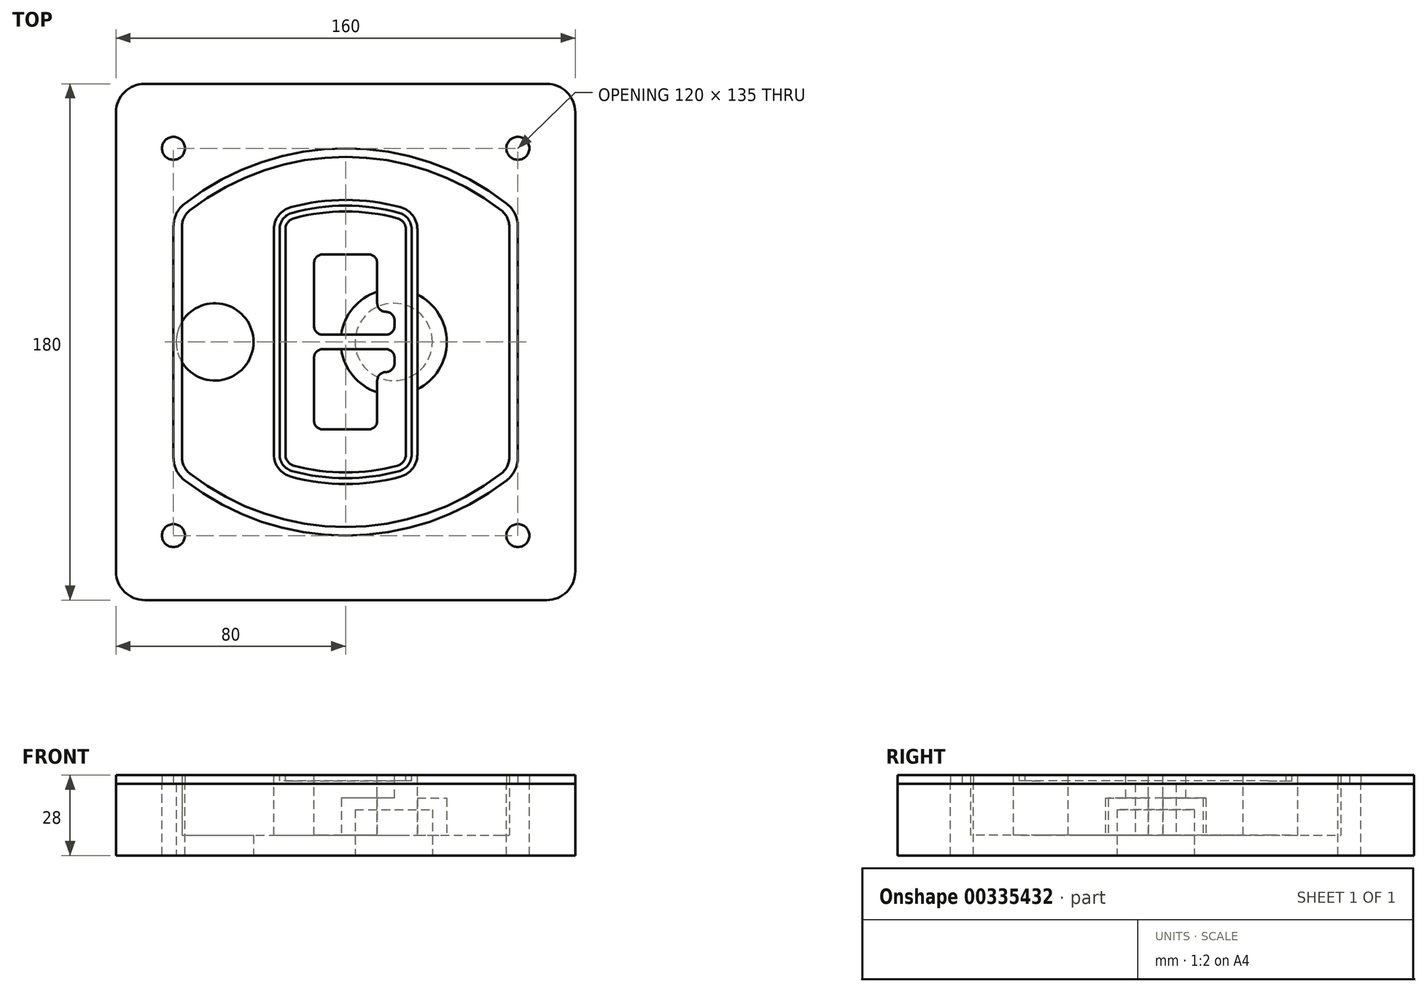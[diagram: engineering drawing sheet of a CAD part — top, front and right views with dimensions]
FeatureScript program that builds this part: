
annotation { "Feature Type Name" : "Feature", "Feature Type Description" : "" }
export const myFeature = defineFeature(function(context is Context, id is Id, definition is map)
    precondition{}
    {
        {
            var Q0;
            Q0=qCreatedBy(makeId("Top.planeOp"),FACE);
            var sketch = newSketch(context, id + "F0", { "sketchPlane" : qUnion([Q0])});
            skPoint(sketch, "E0.rect.middle", {"position": v(0, 0) * mm});
            skLineSegment(sketch, "E1.bottom", {"start": v(-70, -90) * mm, "end": v(70, -90) * mm});
            skLineSegment(sketch, "E1.top", {"start": v(-70, 90) * mm, "end": v(70, 90) * mm});
            skLineSegment(sketch, "E1.left", {"start": v(-80, -80) * mm, "end": v(-80, 80) * mm});
            skLineSegment(sketch, "E1.right", {"start": v(80, -80) * mm, "end": v(80, 80) * mm});
            skLineSegment(sketch, "E2", {"start": v(-80, 90) * mm, "end": v(80, -90) * mm, "construction": true});
            skLineSegment(sketch, "E3", {"start": v(80, 90) * mm, "end": v(-80, -90) * mm, "construction": true});
            skCircle(sketch, "E4", {"center": v(-60, 67.5) * mm, "radius": 4 * mm});
            skCircle(sketch, "E5", {"center": v(60, 67.5) * mm, "radius": 4 * mm});
            skCircle(sketch, "E6", {"center": v(60, -67.5) * mm, "radius": 4 * mm});
            skCircle(sketch, "E7", {"center": v(-60, -67.5) * mm, "radius": 4 * mm});
            skLineSegment(sketch, "E8", {"start": v(-60, 67.5) * mm, "end": v(60, 67.5) * mm, "construction": true});
            skLineSegment(sketch, "E9", {"start": v(60, 67.5) * mm, "end": v(60, -67.5) * mm, "construction": true});
            skLineSegment(sketch, "E10", {"start": v(60, -67.5) * mm, "end": v(-60, -67.5) * mm, "construction": true});
            skLineSegment(sketch, "E11", {"start": v(-60, -67.5) * mm, "end": v(-60, 67.5) * mm, "construction": true});
            skLineSegment(sketch, "E12", {"start": v(-60, 40.3) * mm, "end": v(-60, -40.3) * mm});
            skLineSegment(sketch, "E13", {"start": v(60, 40.3) * mm, "end": v(60, -40.3) * mm});
            skArc(sketch, "E14", {"start": v(56.15, 48.18) * mm, "mid": v(0, 67.5) * mm, "end": v(-56.15, 48.18) * mm});
            skArc(sketch, "E15", {"start": v(-56.15, -48.18) * mm, "mid": v(0, -67.5) * mm, "end": v(56.15, -48.18) * mm});
            skLineSegment(sketch, "E16", {"start": v(-60, 0) * mm, "end": v(60, 0) * mm, "construction": true});
            skPoint(sketch, "E17.visualSharp", {"position": v(-60, -45) * mm});
            skArc(sketch, "E17.filletArc", {"start": v(-60, -40.3) * mm, "mid": v(-58.99, -44.68) * mm, "end": v(-56.15, -48.18) * mm});
            skPoint(sketch, "E18.visualSharp", {"position": v(-60, 45) * mm});
            skArc(sketch, "E18.filletArc", {"start": v(-56.15, 48.18) * mm, "mid": v(-58.99, 44.68) * mm, "end": v(-60, 40.3) * mm});
            skPoint(sketch, "E19.visualSharp", {"position": v(60, 45) * mm});
            skArc(sketch, "E19.filletArc", {"start": v(60, 40.3) * mm, "mid": v(58.99, 44.68) * mm, "end": v(56.15, 48.18) * mm});
            skPoint(sketch, "E20.visualSharp", {"position": v(60, -45) * mm});
            skArc(sketch, "E20.filletArc", {"start": v(56.15, -48.18) * mm, "mid": v(58.99, -44.68) * mm, "end": v(60, -40.3) * mm});
            skPoint(sketch, "E21.visualSharp", {"position": v(-80, 90) * mm});
            skArc(sketch, "E21.filletArc", {"start": v(-70, 90) * mm, "mid": v(-77.07, 87.07) * mm, "end": v(-80, 80) * mm});
            skPoint(sketch, "E22.visualSharp", {"position": v(80, 90) * mm});
            skArc(sketch, "E22.filletArc", {"start": v(80, 80) * mm, "mid": v(77.07, 87.07) * mm, "end": v(70, 90) * mm});
            skPoint(sketch, "E23.visualSharp", {"position": v(80, -90) * mm});
            skArc(sketch, "E23.filletArc", {"start": v(70, -90) * mm, "mid": v(77.07, -87.07) * mm, "end": v(80, -80) * mm});
            skPoint(sketch, "E24.visualSharp", {"position": v(-80, -90) * mm});
            skArc(sketch, "E24.filletArc", {"start": v(-80, -80) * mm, "mid": v(-77.07, -87.07) * mm, "end": v(-70, -90) * mm});
            skArc(sketch, "E25.0", {"start": v(57, 40.3) * mm, "mid": v(56.3, 43.36) * mm, "end": v(54.3, 45.81) * mm});
            skLineSegment(sketch, "E25.1", {"start": v(57, 40.3) * mm, "end": v(57, -40.3) * mm});
            skArc(sketch, "E25.2", {"start": v(54.3, -45.81) * mm, "mid": v(56.3, -43.36) * mm, "end": v(57, -40.3) * mm});
            skArc(sketch, "E25.3", {"start": v(-54.3, -45.81) * mm, "mid": v(0, -64.5) * mm, "end": v(54.3, -45.81) * mm});
            skArc(sketch, "E25.4", {"start": v(-57, -40.3) * mm, "mid": v(-56.3, -43.36) * mm, "end": v(-54.3, -45.81) * mm});
            skArc(sketch, "E25.5", {"start": v(54.3, 45.81) * mm, "mid": v(0, 64.5) * mm, "end": v(-54.3, 45.81) * mm});
            skLineSegment(sketch, "E25.6", {"start": v(-57, 40.3) * mm, "end": v(-57, -40.3) * mm});
            skArc(sketch, "E25.7", {"start": v(-54.3, 45.81) * mm, "mid": v(-56.3, 43.36) * mm, "end": v(-57, 40.3) * mm});
            skArc(sketch, "E26.0", {"start": v(-58.62, 51.33) * mm, "mid": v(-62.58, 46.43) * mm, "end": v(-64, 40.3) * mm});
            skArc(sketch, "E26.1", {"start": v(58.62, 51.33) * mm, "mid": v(0, 71.5) * mm, "end": v(-58.62, 51.33) * mm});
            skArc(sketch, "E26.2", {"start": v(64, 40.3) * mm, "mid": v(62.58, 46.43) * mm, "end": v(58.62, 51.33) * mm});
            skLineSegment(sketch, "E26.3", {"start": v(64, 40.3) * mm, "end": v(64, -40.3) * mm});
            skArc(sketch, "E26.4", {"start": v(58.62, -51.33) * mm, "mid": v(62.58, -46.43) * mm, "end": v(64, -40.3) * mm});
            skLineSegment(sketch, "E26.5", {"start": v(-64, 40.3) * mm, "end": v(-64, -40.3) * mm});
            skArc(sketch, "E26.6", {"start": v(-58.62, -51.33) * mm, "mid": v(0, -71.5) * mm, "end": v(58.62, -51.33) * mm});
            skArc(sketch, "E26.7", {"start": v(-64, -40.3) * mm, "mid": v(-62.58, -46.43) * mm, "end": v(-58.62, -51.33) * mm});
            skSolve(sketch);
        }
        {
            var Q0;
            Q0=makeQuery(id+"F0.imprint","IMPRINT",FACE,{"disambiguationData":[TD([[makeQuery(id+"F0.imprint","IMPRINT",EDGE,{"derivedFrom":sQuery(id+"F0.wireOp",EDGE,"E1.bottom")}),1.0]])]});
            var Q1;
            Q1=makeQuery(id+"F0.imprint","IMPRINT",FACE,{"disambiguationData":[TD([[makeQuery(id+"F0.imprint","IMPRINT",EDGE,{"derivedFrom":sQuery(id+"F0.wireOp",EDGE,"E12")}),1.0]])]});
            var Q2;
            Q2=makeQuery(id+"F0.imprint","IMPRINT",FACE,{"disambiguationData":[TD([[makeQuery(id+"F0.imprint","IMPRINT",EDGE,{"derivedFrom":sQuery(id+"F0.wireOp",EDGE,"E25.0")}),1.0]])]});
            var Q3;
            Q3=makeQuery(id+"F0.imprint","IMPRINT",FACE,{"disambiguationData":[TD([[makeQuery(id+"F0.imprint","IMPRINT",EDGE,{"derivedFrom":sQuery(id+"F0.wireOp",EDGE,"E12")}),-1.0]])]});
            extrude(context, id + "F1", {"entities" : qUnion([Q0, Q1, Q2, Q3]), "oppositeDirection" : true, "depth" : 25 * mm});
        }
        {
            var Q0;
            Q0=makeQuery(id+"F0.imprint","IMPRINT",FACE,{"disambiguationData":[TD([[makeQuery(id+"F0.imprint","IMPRINT",EDGE,{"derivedFrom":sQuery(id+"F0.wireOp",EDGE,"E12")}),1.0]])]});
            extrude(context, id + "F2", {"entities" : qUnion([Q0]), "operationType" : NewBodyOperationType.ADD, "depth" : 3 * mm});
        }
        {
            var Q0;
            Q0=makeQuery(id+"F0.imprint","IMPRINT",FACE,{"disambiguationData":[TD([[makeQuery(id+"F0.imprint","IMPRINT",EDGE,{"derivedFrom":sQuery(id+"F0.wireOp",EDGE,"E25.0")}),1.0]])]});
            extrude(context, id + "F3", {"entities" : qUnion([Q0]), "operationType" : NewBodyOperationType.REMOVE, "oppositeDirection" : true, "depth" : 18 * mm});
        }
        {
            var Q0;
            Q0=makeQuery(id+"F2.opExtrude","CAP_FACE",FACE,{"disambiguationData":[OSD([sQuery(id+"F0.wireOp",EDGE,"E12"),sQuery(id+"F0.wireOp",EDGE,"E13"),sQuery(id+"F0.wireOp",EDGE,"E14"),sQuery(id+"F0.wireOp",EDGE,"E15"),sQuery(id+"F0.wireOp",EDGE,"E17.filletArc"),sQuery(id+"F0.wireOp",EDGE,"E18.filletArc"),sQuery(id+"F0.wireOp",EDGE,"E19.filletArc"),sQuery(id+"F0.wireOp",EDGE,"E20.filletArc"),sQuery(id+"F0.wireOp",EDGE,"E25.0"),sQuery(id+"F0.wireOp",EDGE,"E25.1"),sQuery(id+"F0.wireOp",EDGE,"E25.2"),sQuery(id+"F0.wireOp",EDGE,"E25.3"),sQuery(id+"F0.wireOp",EDGE,"E25.4"),sQuery(id+"F0.wireOp",EDGE,"E25.5"),sQuery(id+"F0.wireOp",EDGE,"E25.6"),sQuery(id+"F0.wireOp",EDGE,"E25.7")])],"isStart":false});
            var sketch = newSketch(context, id + "F4", { "sketchPlane" : qUnion([Q0])});
            skArc(sketch, "E27.0", {"start": v(-19.08, -46.97) * mm, "mid": v(0, -49.5) * mm, "end": v(19.08, -46.97) * mm});
            skArc(sketch, "E28.0", {"start": v(19.08, 46.97) * mm, "mid": v(0, 49.5) * mm, "end": v(-19.08, 46.97) * mm});
            skLineSegment(sketch, "E29", {"start": v(-25, 39.25) * mm, "end": v(-25, -39.25) * mm});
            skLineSegment(sketch, "E30", {"start": v(25, 39.25) * mm, "end": v(25, -39.25) * mm});
            skLineSegment(sketch, "E31", {"start": v(-25, 45.1) * mm, "end": v(25, 45.1) * mm, "construction": true});
            skLineSegment(sketch, "E32", {"start": v(-25, -45.1) * mm, "end": v(25, -45.1) * mm, "construction": true});
            skPoint(sketch, "E33.visualSharp", {"position": v(-25, 45.1) * mm});
            skArc(sketch, "E33.filletArc", {"start": v(-19.08, 46.97) * mm, "mid": v(-23.35, 44.11) * mm, "end": v(-25, 39.25) * mm});
            skPoint(sketch, "E34.visualSharp", {"position": v(25, 45.1) * mm});
            skArc(sketch, "E34.filletArc", {"start": v(25, 39.25) * mm, "mid": v(23.35, 44.11) * mm, "end": v(19.08, 46.97) * mm});
            skPoint(sketch, "E35.visualSharp", {"position": v(25, -45.1) * mm});
            skArc(sketch, "E35.filletArc", {"start": v(19.08, -46.97) * mm, "mid": v(23.35, -44.11) * mm, "end": v(25, -39.25) * mm});
            skPoint(sketch, "E36.visualSharp", {"position": v(-25, -45.1) * mm});
            skArc(sketch, "E36.filletArc", {"start": v(-25, -39.25) * mm, "mid": v(-23.35, -44.11) * mm, "end": v(-19.08, -46.97) * mm});
            skArc(sketch, "E37.0", {"start": v(54.3, 45.81) * mm, "mid": v(0, 64.5) * mm, "end": v(-54.3, 45.81) * mm});
            skArc(sketch, "E37.1", {"start": v(-54.3, 45.81) * mm, "mid": v(-56.3, 43.36) * mm, "end": v(-57, 40.3) * mm});
            skLineSegment(sketch, "E37.2", {"start": v(-57, 40.3) * mm, "end": v(-57, -40.3) * mm});
            skArc(sketch, "E37.3", {"start": v(-57, -40.3) * mm, "mid": v(-56.3, -43.36) * mm, "end": v(-54.3, -45.81) * mm});
            skArc(sketch, "E37.4", {"start": v(-54.3, -45.81) * mm, "mid": v(0, -64.5) * mm, "end": v(54.3, -45.81) * mm});
            skArc(sketch, "E37.5", {"start": v(54.3, -45.81) * mm, "mid": v(56.3, -43.36) * mm, "end": v(57, -40.3) * mm});
            skLineSegment(sketch, "E37.6", {"start": v(57, 40.3) * mm, "end": v(57, -40.3) * mm});
            skArc(sketch, "E37.7", {"start": v(57, 40.3) * mm, "mid": v(56.3, 43.36) * mm, "end": v(54.3, 45.81) * mm});
            skLineSegment(sketch, "E38.0", {"start": v(23, 39.25) * mm, "end": v(23, -39.25) * mm});
            skArc(sketch, "E38.1", {"start": v(18.56, -45.04) * mm, "mid": v(21.76, -42.9) * mm, "end": v(23, -39.25) * mm});
            skArc(sketch, "E38.2", {"start": v(-18.56, -45.04) * mm, "mid": v(0, -47.5) * mm, "end": v(18.56, -45.04) * mm});
            skArc(sketch, "E38.3", {"start": v(-23, -39.25) * mm, "mid": v(-21.76, -42.9) * mm, "end": v(-18.56, -45.04) * mm});
            skLineSegment(sketch, "E38.4", {"start": v(-23, 39.25) * mm, "end": v(-23, -39.25) * mm});
            skArc(sketch, "E38.5", {"start": v(23, 39.25) * mm, "mid": v(21.76, 42.9) * mm, "end": v(18.56, 45.04) * mm});
            skArc(sketch, "E38.6", {"start": v(-18.56, 45.04) * mm, "mid": v(-21.76, 42.9) * mm, "end": v(-23, 39.25) * mm});
            skArc(sketch, "E38.7", {"start": v(18.56, 45.04) * mm, "mid": v(0, 47.5) * mm, "end": v(-18.56, 45.04) * mm});
            skArc(sketch, "E39.0", {"start": v(21, 39.25) * mm, "mid": v(20.18, 41.68) * mm, "end": v(18.04, 43.1) * mm});
            skLineSegment(sketch, "E39.1", {"start": v(21, 39.25) * mm, "end": v(21, -39.25) * mm});
            skArc(sketch, "E39.2", {"start": v(18.04, -43.1) * mm, "mid": v(20.18, -41.68) * mm, "end": v(21, -39.25) * mm});
            skArc(sketch, "E39.3", {"start": v(-18.04, -43.1) * mm, "mid": v(0, -45.5) * mm, "end": v(18.04, -43.1) * mm});
            skArc(sketch, "E39.4", {"start": v(-21, -39.25) * mm, "mid": v(-20.18, -41.68) * mm, "end": v(-18.04, -43.1) * mm});
            skArc(sketch, "E39.5", {"start": v(18.04, 43.1) * mm, "mid": v(0, 45.5) * mm, "end": v(-18.04, 43.1) * mm});
            skLineSegment(sketch, "E39.6", {"start": v(-21, 39.25) * mm, "end": v(-21, -39.25) * mm});
            skArc(sketch, "E39.7", {"start": v(-18.04, 43.1) * mm, "mid": v(-20.18, 41.68) * mm, "end": v(-21, 39.25) * mm});
            skLineSegment(sketch, "E40", {"start": v(-25, 0) * mm, "end": v(25, 0) * mm, "construction": true});
            skLineSegment(sketch, "E41", {"start": v(-11, 5.5) * mm, "end": v(-11, 27.5) * mm});
            skLineSegment(sketch, "E42", {"start": v(-8, 30.5) * mm, "end": v(8, 30.5) * mm});
            skLineSegment(sketch, "E43", {"start": v(11, 27.5) * mm, "end": v(11, 13.5) * mm});
            skLineSegment(sketch, "E44", {"start": v(14, 10.5) * mm, "end": v(14, 10.5) * mm});
            skLineSegment(sketch, "E45", {"start": v(17, 7.5) * mm, "end": v(17, 5.5) * mm});
            skLineSegment(sketch, "E46", {"start": v(14, 2.5) * mm, "end": v(-8, 2.5) * mm});
            skPoint(sketch, "E47.visualSharp", {"position": v(-11, 30.5) * mm});
            skArc(sketch, "E47.filletArc", {"start": v(-8, 30.5) * mm, "mid": v(-10.12, 29.62) * mm, "end": v(-11, 27.5) * mm});
            skPoint(sketch, "E48.visualSharp", {"position": v(11, 30.5) * mm});
            skArc(sketch, "E48.filletArc", {"start": v(11, 27.5) * mm, "mid": v(10.12, 29.62) * mm, "end": v(8, 30.5) * mm});
            skPoint(sketch, "E49.visualSharp", {"position": v(11, 10.5) * mm});
            skArc(sketch, "E49.filletArc", {"start": v(11, 13.5) * mm, "mid": v(11.88, 11.38) * mm, "end": v(14, 10.5) * mm});
            skPoint(sketch, "E50.visualSharp", {"position": v(17, 10.5) * mm});
            skArc(sketch, "E50.filletArc", {"start": v(17, 7.5) * mm, "mid": v(16.12, 9.62) * mm, "end": v(14, 10.5) * mm});
            skPoint(sketch, "E51.visualSharp", {"position": v(17, 2.5) * mm});
            skArc(sketch, "E51.filletArc", {"start": v(14, 2.5) * mm, "mid": v(16.12, 3.38) * mm, "end": v(17, 5.5) * mm});
            skPoint(sketch, "E52.visualSharp", {"position": v(-11, 2.5) * mm});
            skArc(sketch, "E52.filletArc", {"start": v(-11, 5.5) * mm, "mid": v(-10.12, 3.38) * mm, "end": v(-8, 2.5) * mm});
            skLineSegment(sketch, "E53.0.MirrorCS", {"start": v(14, -2.5) * mm, "end": v(-8, -2.5) * mm});
            skArc(sketch, "E54.0.MirrorCS", {"start": v(-11, -5.5) * mm, "mid": v(-10.12, -3.38) * mm, "end": v(-8, -2.5) * mm});
            skLineSegment(sketch, "E55.0.MirrorCS", {"start": v(-11, -5.5) * mm, "end": v(-11, -27.5) * mm});
            skArc(sketch, "E56.0.MirrorCS", {"start": v(-8, -30.5) * mm, "mid": v(-10.12, -29.62) * mm, "end": v(-11, -27.5) * mm});
            skLineSegment(sketch, "E57.0.MirrorCS", {"start": v(-8, -30.5) * mm, "end": v(8, -30.5) * mm});
            skArc(sketch, "E58.0.MirrorCS", {"start": v(11, -27.5) * mm, "mid": v(10.12, -29.62) * mm, "end": v(8, -30.5) * mm});
            skLineSegment(sketch, "E59.0.MirrorCS", {"start": v(11, -27.5) * mm, "end": v(11, -13.5) * mm});
            skArc(sketch, "E60.0.MirrorCS", {"start": v(11, -13.5) * mm, "mid": v(11.88, -11.38) * mm, "end": v(14, -10.5) * mm});
            skArc(sketch, "E61.0.MirrorCS", {"start": v(17, -7.5) * mm, "mid": v(16.12, -9.62) * mm, "end": v(14, -10.5) * mm});
            skLineSegment(sketch, "E62.0.MirrorCS", {"start": v(17, -7.5) * mm, "end": v(17, -5.5) * mm});
            skArc(sketch, "E63.0.MirrorCS", {"start": v(14, -2.5) * mm, "mid": v(16.12, -3.38) * mm, "end": v(17, -5.5) * mm});
            skSolve(sketch);
        }
        {
            var Q0;
            Q0=makeQuery(id+"F4.imprint","IMPRINT",FACE,{"disambiguationData":[TD([[makeQuery(id+"F4.imprint","IMPRINT",EDGE,{"derivedFrom":sQuery(id+"F4.wireOp",EDGE,"E27.0")}),1.0]])]});
            var Q1;
            Q1=makeQuery(id+"F4.imprint","IMPRINT",FACE,{"disambiguationData":[TD([[makeQuery(id+"F4.imprint","IMPRINT",EDGE,{"derivedFrom":sQuery(id+"F4.wireOp",EDGE,"E38.0")}),-1.0]])]});
            var Q2;
            Q2=makeQuery(id+"F4.imprint","IMPRINT",FACE,{"disambiguationData":[TD([[makeQuery(id+"F4.imprint","IMPRINT",EDGE,{"derivedFrom":sQuery(id+"F4.wireOp",EDGE,"E39.0")}),1.0]])]});
            extrude(context, id + "F5", {"entities" : qUnion([Q0, Q1, Q2]), "operationType" : NewBodyOperationType.ADD, "endBound" : BoundingType.UP_TO_NEXT, "oppositeDirection" : true, "depth" : 25 * mm});
        }
        {
            var Q0;
            Q0=makeQuery(id+"F4.imprint","IMPRINT",FACE,{"disambiguationData":[TD([[makeQuery(id+"F4.imprint","IMPRINT",EDGE,{"derivedFrom":sQuery(id+"F4.wireOp",EDGE,"E38.0")}),-1.0]])]});
            extrude(context, id + "F6", {"entities" : qUnion([Q0]), "operationType" : NewBodyOperationType.REMOVE, "oppositeDirection" : true, "depth" : 2 * mm});
        }
        {
            var Q0;
            Q0=makeQuery(id+"F1.opExtrude","CAP_FACE",FACE,{"disambiguationData":[OSD([sQuery(id+"F0.wireOp",EDGE,"E1.bottom"),sQuery(id+"F0.wireOp",EDGE,"E1.top"),sQuery(id+"F0.wireOp",EDGE,"E1.left"),sQuery(id+"F0.wireOp",EDGE,"E1.right"),sQuery(id+"F0.wireOp",EDGE,"E4"),sQuery(id+"F0.wireOp",EDGE,"E5"),sQuery(id+"F0.wireOp",EDGE,"E6"),sQuery(id+"F0.wireOp",EDGE,"E7"),sQuery(id+"F0.wireOp",EDGE,"E21.filletArc"),sQuery(id+"F0.wireOp",EDGE,"E22.filletArc"),sQuery(id+"F0.wireOp",EDGE,"E23.filletArc"),sQuery(id+"F0.wireOp",EDGE,"E24.filletArc")])],"isStart":false});
            var sketch = newSketch(context, id + "F7", { "sketchPlane" : qUnion([Q0])});
            skCircle(sketch, "E64", {"center": v(16.76, 0) * mm, "radius": 13.47 * mm});
            skCircle(sketch, "E65", {"center": v(-45.56, 0) * mm, "radius": 13.47 * mm});
            skLineSegment(sketch, "E66", {"start": v(80, 0) * mm, "end": v(-80, 0) * mm});
            skCircle(sketch, "E67", {"center": v(16.76, 0) * mm, "radius": 18.47 * mm});
            skCircle(sketch, "E68", {"center": v(60, -67.5) * mm, "radius": 6 * mm});
            skCircle(sketch, "E69", {"center": v(-60, -67.5) * mm, "radius": 6 * mm});
            skCircle(sketch, "E70", {"center": v(-60, 67.5) * mm, "radius": 6 * mm});
            skCircle(sketch, "E71", {"center": v(60, 67.5) * mm, "radius": 6 * mm});
            skSolve(sketch);
        }
        {
            var Q0;
            {var subQ1=sQuery(id+"F7.wireOp",EDGE,"E66");var subQ4=sQuery(id+"F7.wireOp",EDGE,"E64");var subQ6=makeQuery(id+"F7.imprint","INTERSECT",VERTEX,{"disambiguationData":[OD(0.0)],"derivedFrom":[subQ4,subQ1]});Q0=makeQuery(id+"F7.imprint","IMPRINT",FACE,{"disambiguationData":[TD([[makeQuery(id+"F7.imprint","IMPRINT",EDGE,{"disambiguationData":[TD([[subQ6,-1.0]])],"derivedFrom":subQ4}),-1.0]])]});}
            var Q1;
            {var subQ0=sQuery(id+"F7.wireOp",EDGE,"E66");var subQ1=sQuery(id+"F7.wireOp",EDGE,"E64");var subQ3=makeQuery(id+"F7.imprint","INTERSECT",VERTEX,{"disambiguationData":[OD(0.0)],"derivedFrom":[subQ1,subQ0]});Q1=makeQuery(id+"F7.imprint","IMPRINT",FACE,{"disambiguationData":[TD([[makeQuery(id+"F7.imprint","IMPRINT",EDGE,{"disambiguationData":[TD([[subQ3,-1.0]])],"derivedFrom":subQ1}),1.0]])]});}
            var Q2;
            {var subQ0=sQuery(id+"F7.wireOp",EDGE,"E66");var subQ1=sQuery(id+"F7.wireOp",EDGE,"E64");var subQ3=makeQuery(id+"F7.imprint","INTERSECT",VERTEX,{"disambiguationData":[OD(0.0)],"derivedFrom":[subQ1,subQ0]});Q2=makeQuery(id+"F7.imprint","IMPRINT",FACE,{"disambiguationData":[TD([[makeQuery(id+"F7.imprint","IMPRINT",EDGE,{"disambiguationData":[TD([[subQ3,1.0]])],"derivedFrom":subQ1}),1.0]])]});}
            var Q3;
            {var subQ1=sQuery(id+"F7.wireOp",EDGE,"E66");var subQ4=sQuery(id+"F7.wireOp",EDGE,"E64");var subQ6=makeQuery(id+"F7.imprint","INTERSECT",VERTEX,{"disambiguationData":[OD(0.0)],"derivedFrom":[subQ4,subQ1]});Q3=makeQuery(id+"F7.imprint","IMPRINT",FACE,{"disambiguationData":[TD([[makeQuery(id+"F7.imprint","IMPRINT",EDGE,{"disambiguationData":[TD([[subQ6,1.0]])],"derivedFrom":subQ4}),-1.0]])]});}
            extrude(context, id + "F8", {"entities" : qUnion([Q0, Q1, Q2, Q3]), "operationType" : NewBodyOperationType.ADD, "oppositeDirection" : true, "depth" : 20 * mm});
        }
        {
            var Q0;
            {var subQ0=sQuery(id+"F7.wireOp",EDGE,"E66");var subQ1=sQuery(id+"F7.wireOp",EDGE,"E64");var subQ3=makeQuery(id+"F7.imprint","INTERSECT",VERTEX,{"disambiguationData":[OD(0.0)],"derivedFrom":[subQ1,subQ0]});Q0=makeQuery(id+"F7.imprint","IMPRINT",FACE,{"disambiguationData":[TD([[makeQuery(id+"F7.imprint","IMPRINT",EDGE,{"disambiguationData":[TD([[subQ3,-1.0]])],"derivedFrom":subQ1}),1.0]])]});}
            var Q1;
            {var subQ0=sQuery(id+"F7.wireOp",EDGE,"E66");var subQ1=sQuery(id+"F7.wireOp",EDGE,"E64");var subQ3=makeQuery(id+"F7.imprint","INTERSECT",VERTEX,{"disambiguationData":[OD(0.0)],"derivedFrom":[subQ1,subQ0]});Q1=makeQuery(id+"F7.imprint","IMPRINT",FACE,{"disambiguationData":[TD([[makeQuery(id+"F7.imprint","IMPRINT",EDGE,{"disambiguationData":[TD([[subQ3,1.0]])],"derivedFrom":subQ1}),1.0]])]});}
            extrude(context, id + "F9", {"entities" : qUnion([Q0, Q1]), "operationType" : NewBodyOperationType.REMOVE, "oppositeDirection" : true, "depth" : 16 * mm});
        }
        {
            var Q0;
            {var subQ0=sQuery(id+"F7.wireOp",EDGE,"E66");var subQ1=sQuery(id+"F7.wireOp",EDGE,"E65");var subQ3=makeQuery(id+"F7.imprint","INTERSECT",VERTEX,{"disambiguationData":[OD(0.0)],"derivedFrom":[subQ1,subQ0]});Q0=makeQuery(id+"F7.imprint","IMPRINT",FACE,{"disambiguationData":[TD([[makeQuery(id+"F7.imprint","IMPRINT",EDGE,{"disambiguationData":[TD([[subQ3,-1.0]])],"derivedFrom":subQ1}),1.0]])]});}
            var Q1;
            {var subQ0=sQuery(id+"F7.wireOp",EDGE,"E66");var subQ1=sQuery(id+"F7.wireOp",EDGE,"E65");var subQ3=makeQuery(id+"F7.imprint","INTERSECT",VERTEX,{"disambiguationData":[OD(0.0)],"derivedFrom":[subQ1,subQ0]});Q1=makeQuery(id+"F7.imprint","IMPRINT",FACE,{"disambiguationData":[TD([[makeQuery(id+"F7.imprint","IMPRINT",EDGE,{"disambiguationData":[TD([[subQ3,1.0]])],"derivedFrom":subQ1}),1.0]])]});}
            extrude(context, id + "F10", {"entities" : qUnion([Q0, Q1]), "operationType" : NewBodyOperationType.REMOVE, "oppositeDirection" : true, "depth" : 25 * mm});
        }
        {
            var Q0;
            {var subQ0=sQuery(id+"F0.wireOp",EDGE,"E21.filletArc");var subQ1=sQuery(id+"F0.wireOp",EDGE,"E7");var subQ2=sQuery(id+"F0.wireOp",EDGE,"E6");var subQ3=sQuery(id+"F0.wireOp",EDGE,"E5");var subQ4=sQuery(id+"F0.wireOp",EDGE,"E4");var subQ5=sQuery(id+"F0.wireOp",EDGE,"E22.filletArc");var subQ6=sQuery(id+"F0.wireOp",EDGE,"E1.bottom");var subQ7=sQuery(id+"F0.wireOp",EDGE,"E1.right");var subQ8=sQuery(id+"F0.wireOp",EDGE,"E1.top");var subQ9=sQuery(id+"F0.wireOp",EDGE,"E1.left");var subQ10=sQuery(id+"F0.wireOp",EDGE,"E23.filletArc");var subQ11=sQuery(id+"F0.wireOp",EDGE,"E24.filletArc");Q0=makeQuery(id+"F2.boolean.opBoolean","SPLIT",FACE,{"disambiguationData":[TD([makeQuery(id+"F1.opExtrude","SWEPT_FACE",FACE,{"disambiguationData":[OSD([subQ6])]})])],"derivedFrom":makeQuery(id+"F1.opExtrude","CAP_FACE",FACE,{"disambiguationData":[OSD([subQ6,subQ8,subQ9,subQ7,subQ4,subQ3,subQ2,subQ1,subQ0,subQ5,subQ10,subQ11])],"isStart":true})});}
            var sketch = newSketch(context, id + "F11", { "sketchPlane" : qUnion([Q0])});
            skLineSegment(sketch, "E72", {"start": v(0, 90) * mm, "end": v(0, 120) * mm, "construction": true});
            skPoint(sketch, "E72.endSnap0", {"position": v(0, 90) * mm});
            skLineSegment(sketch, "E73", {"start": v(-15, 120) * mm, "end": v(-15, 108) * mm});
            skLineSegment(sketch, "E74", {"start": v(-15, 108) * mm, "end": v(-15, 120) * mm});
            skLineSegment(sketch, "E75", {"start": v(15, 120) * mm, "end": v(15, 108) * mm});
            skLineSegment(sketch, "E76", {"start": v(15, 108) * mm, "end": v(33, 90) * mm});
            skLineSegment(sketch, "E77", {"start": v(-15, 108) * mm, "end": v(-33, 90) * mm});
            skCircle(sketch, "E78", {"center": v(0, 120) * mm, "radius": 6 * mm});
            skLineSegment(sketch, "E79", {"start": v(0, -3.3) * mm, "end": v(0, 0) * mm});
            skLineSegment(sketch, "E80", {"start": v(-80, 0) * mm, "end": v(77.56, 0) * mm, "construction": true});
            skPoint(sketch, "E80.endSnap0", {"position": v(80, 0) * mm});
            skArc(sketch, "E81", {"start": v(15, 120) * mm, "mid": v(0, 135) * mm, "end": v(-15, 120) * mm});
            skArc(sketch, "E82.MirrorCS", {"start": v(15, -120) * mm, "mid": v(0, -135) * mm, "end": v(-15, -120) * mm});
            skLineSegment(sketch, "E83.MirrorCS", {"start": v(-15, -108) * mm, "end": v(-15, -120) * mm});
            skLineSegment(sketch, "E84.MirrorCS", {"start": v(15, -108) * mm, "end": v(33, -90) * mm});
            skLineSegment(sketch, "E85.MirrorCS", {"start": v(15, -120) * mm, "end": v(15, -108) * mm});
            skLineSegment(sketch, "E86.MirrorCS", {"start": v(-15, -108) * mm, "end": v(-33, -90) * mm});
            skCircle(sketch, "E87.MirrorC", {"center": v(0, -120) * mm, "radius": 6 * mm});
            skLineSegment(sketch, "E88.MirrorCS", {"start": v(0, -90) * mm, "end": v(0, -120) * mm, "construction": true});
            skSolve(sketch);
        }
        {
            var Q0;
            Q0=makeQuery(id+"F11.imprint","IMPRINT",FACE,{"disambiguationData":[TD([[makeQuery(id+"F11.imprint","IMPRINT",EDGE,{"derivedFrom":sQuery(id+"F11.wireOp",EDGE,"E74")}),-1.0]])]});
            var Q1;
            Q1=makeQuery(id+"F11.imprint","IMPRINT",FACE,{"disambiguationData":[TD([[makeQuery(id+"F11.imprint","IMPRINT",EDGE,{"derivedFrom":makeQuery(id+"F1.opExtrude","CAP_EDGE",EDGE,{"disambiguationData":[OSD([sQuery(id+"F0.wireOp",EDGE,"E1.left")])],"isStart":true})}),-1.0]])]});
            var Q2;
            Q2=makeQuery(id+"F11.imprint","IMPRINT",FACE,{"disambiguationData":[TD([[makeQuery(id+"F11.imprint","IMPRINT",EDGE,{"derivedFrom":sQuery(id+"F11.wireOp",EDGE,"E82.MirrorCS")}),-1.0]])]});
            var Q3;
            Q3=makeQuery(id+"F2.opExtrude","CAP_FACE",FACE,{"disambiguationData":[OSD([sQuery(id+"F0.wireOp",EDGE,"E12"),sQuery(id+"F0.wireOp",EDGE,"E13"),sQuery(id+"F0.wireOp",EDGE,"E14"),sQuery(id+"F0.wireOp",EDGE,"E15"),sQuery(id+"F0.wireOp",EDGE,"E17.filletArc"),sQuery(id+"F0.wireOp",EDGE,"E18.filletArc"),sQuery(id+"F0.wireOp",EDGE,"E19.filletArc"),sQuery(id+"F0.wireOp",EDGE,"E20.filletArc"),sQuery(id+"F0.wireOp",EDGE,"E25.0"),sQuery(id+"F0.wireOp",EDGE,"E25.1"),sQuery(id+"F0.wireOp",EDGE,"E25.2"),sQuery(id+"F0.wireOp",EDGE,"E25.3"),sQuery(id+"F0.wireOp",EDGE,"E25.4"),sQuery(id+"F0.wireOp",EDGE,"E25.5"),sQuery(id+"F0.wireOp",EDGE,"E25.6"),sQuery(id+"F0.wireOp",EDGE,"E25.7")])],"isStart":false});
            extrude(context, id + "F12", {"entities" : qUnion([Q0, Q1, Q2]), "endBound" : BoundingType.UP_TO_SURFACE, "endBoundEntityFace" : qUnion([Q3]), "depth" : 25 * mm});
        }
    });
